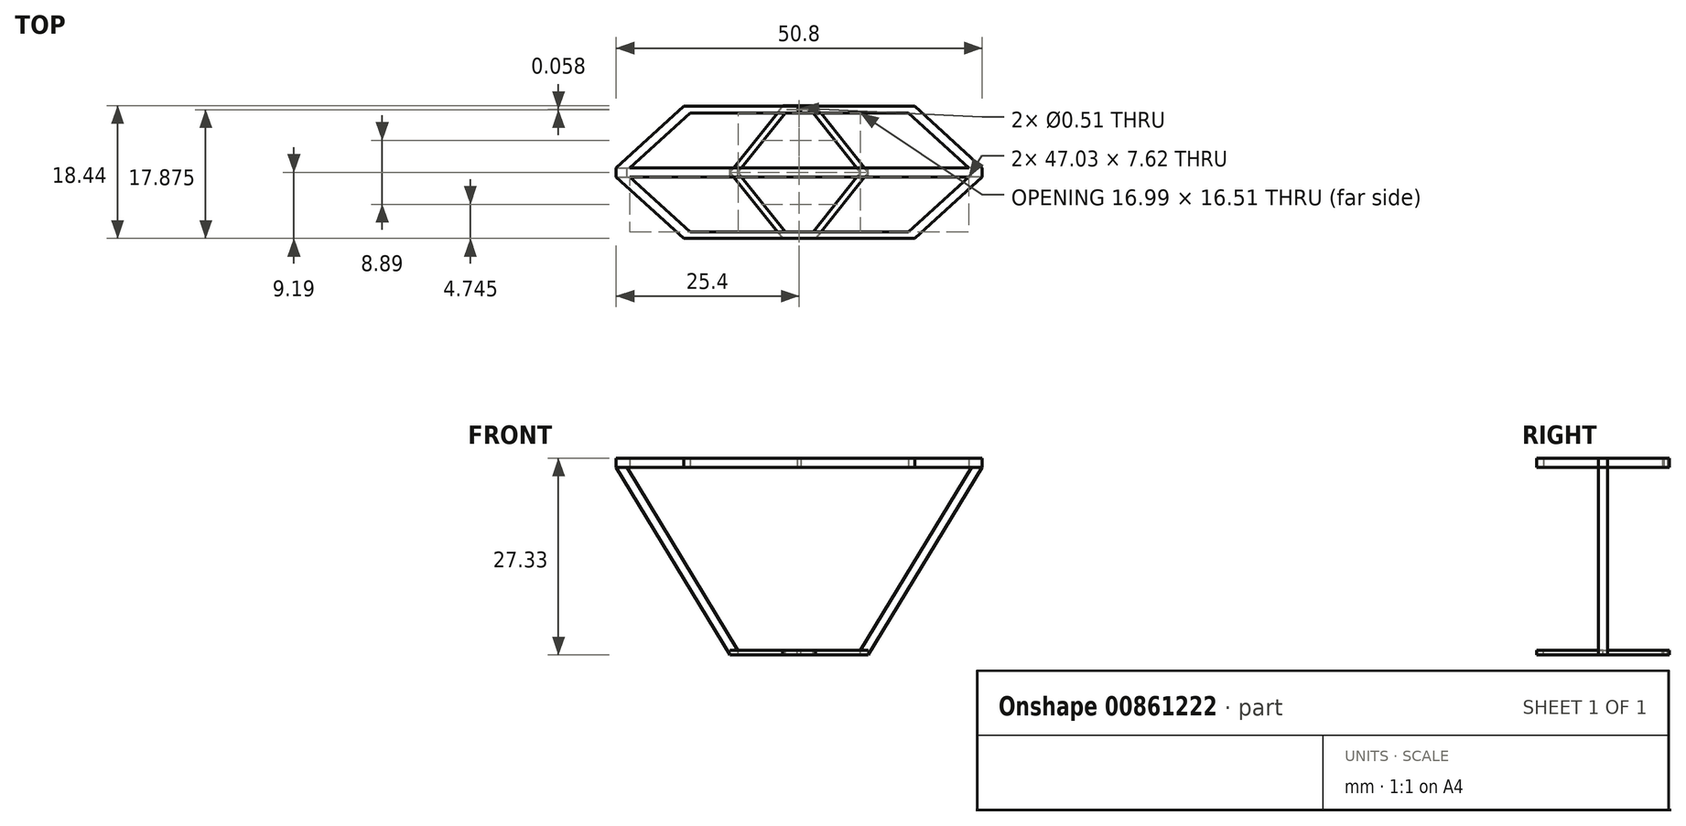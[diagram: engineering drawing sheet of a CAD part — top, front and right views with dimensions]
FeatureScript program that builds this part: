
annotation { "Feature Type Name" : "Feature", "Feature Type Description" : "" }
export const myFeature = defineFeature(function(context is Context, id is Id, definition is map)
    precondition{}
    {
        {
            var Q0;
            Q0=qCreatedBy(makeId("Top.planeOp"),FACE);
            var sketch = newSketch(context, id + "F0", { "sketchPlane" : qUnion([Q0])});
            skLineSegment(sketch, "E0.bottom", {"start": v(23.52, -0.63) * mm, "end": v(-23.52, -0.64) * mm});
            skLineSegment(sketch, "E0.top", {"start": v(23.52, 0.64) * mm, "end": v(-23.52, 0.63) * mm});
            skLineSegment(sketch, "E0.left", {"start": v(25.4, -0.63) * mm, "end": v(25.4, 0.64) * mm});
            skLineSegment(sketch, "E0.right", {"start": v(-25.4, -0.64) * mm, "end": v(-25.4, 0.63) * mm});
            skPoint(sketch, "E0.middle", {"position": v(0, 0) * mm});
            skLineSegment(sketch, "E1", {"start": v(25.4, 0.63) * mm, "end": v(16.02, 9.2) * mm});
            skLineSegment(sketch, "E2", {"start": v(23.52, 0.63) * mm, "end": v(15.16, 8.26) * mm});
            skLineSegment(sketch, "E3", {"start": v(-23.52, 0.63) * mm, "end": v(-15.16, 8.26) * mm});
            skLineSegment(sketch, "E4", {"start": v(-25.4, 0.63) * mm, "end": v(-16.02, 9.2) * mm});
            skLineSegment(sketch, "E5", {"start": v(-15.16, 8.26) * mm, "end": v(15.16, 8.25) * mm});
            skLineSegment(sketch, "E6", {"start": v(16.02, 9.2) * mm, "end": v(-16.02, 9.2) * mm});
            skLineSegment(sketch, "E7", {"start": v(-23.52, -0.63) * mm, "end": v(-15.16, -8.26) * mm});
            skLineSegment(sketch, "E8", {"start": v(-25.4, -0.63) * mm, "end": v(-16.02, -9.2) * mm});
            skLineSegment(sketch, "E9", {"start": v(25.4, -0.63) * mm, "end": v(16.02, -9.2) * mm});
            skLineSegment(sketch, "E10", {"start": v(23.52, -0.63) * mm, "end": v(15.16, -8.25) * mm});
            skLineSegment(sketch, "E11", {"start": v(-15.16, -8.26) * mm, "end": v(15.16, -8.25) * mm});
            skLineSegment(sketch, "E12", {"start": v(-16.02, -9.2) * mm, "end": v(16.02, -9.2) * mm});
            skCircle(sketch, "E13", {"center": v(0, 8.69) * mm, "radius": 0.25 * mm});
            skSolve(sketch);
        }
        {
            var Q0;
            Q0 = qSketchRegion(id + "F0", true);
            extrude(context, id + "F1", {"entities" : qUnion([Q0]), "depth" : 1.27 * mm, "offsetDistance" : 25.4 * mm});
        }
        {
            var Q0;
            Q0=qCreatedBy(makeId("Front.planeOp"),FACE);
            var sketch = newSketch(context, id + "F2", { "sketchPlane" : qUnion([Q0])});
            skLineSegment(sketch, "E14", {"start": v(-25.4, 0) * mm, "end": v(-9.59, -26.06) * mm});
            skLineSegment(sketch, "E15", {"start": v(-23.91, 0) * mm, "end": v(-8.5, -25.4) * mm});
            skLineSegment(sketch, "E16", {"start": v(-25.4, 0) * mm, "end": v(-23.91, 0) * mm});
            skLineSegment(sketch, "E17", {"start": v(25.4, 0) * mm, "end": v(9.59, -26.06) * mm});
            skLineSegment(sketch, "E18", {"start": v(23.91, 0) * mm, "end": v(8.5, -25.4) * mm});
            skLineSegment(sketch, "E19", {"start": v(25.4, 0) * mm, "end": v(23.91, 0) * mm});
            skLineSegment(sketch, "E20", {"start": v(-8.5, -25.4) * mm, "end": v(8.5, -25.4) * mm});
            skLineSegment(sketch, "E21", {"start": v(-9.59, -26.06) * mm, "end": v(9.59, -26.06) * mm});
            skSolve(sketch);
        }
        {
            var Q0;
            Q0 = qSketchRegion(id + "F2", true);
            extrude(context, id + "F3", {"entities" : qUnion([Q0]), "endBound" : BoundingType.SYMMETRIC, "depth" : 1.27 * mm, "offsetDistance" : 25.4 * mm});
        }
        {
            var Q0;
            Q0=qCreatedBy(makeId("Top.planeOp"),FACE);
            cPlane(context, id + "F4", {"entities" : qUnion([Q0]), "cplaneType" : CPlaneType.OFFSET, "offset" : 25.4 * mm, "oppositeDirection" : true, "width" : 152.4 * mm, "height" : 152.4 * mm});
        }
        {
            var Q0;
            Q0=qCreatedBy(id+"F4.planeOp",FACE);
            var sketch = newSketch(context, id + "F5", { "sketchPlane" : qUnion([Q0])});
            skLineSegment(sketch, "E22", {"start": v(8.5, 0) * mm, "end": v(1.93, 8.26) * mm});
            skLineSegment(sketch, "E23", {"start": v(9.59, 0) * mm, "end": v(2.6, 8.78) * mm});
            skLineSegment(sketch, "E24", {"start": v(-8.5, 0) * mm, "end": v(-1.93, 8.26) * mm});
            skLineSegment(sketch, "E25", {"start": v(-9.59, 0) * mm, "end": v(-3.02, 8.26) * mm});
            skLineSegment(sketch, "E26", {"start": v(-1.93, 8.26) * mm, "end": v(1.93, 8.26) * mm});
            skLineSegment(sketch, "E27", {"start": v(2.6, 8.78) * mm, "end": v(2.23, 9.25) * mm});
            skLineSegment(sketch, "E28", {"start": v(-0.69, 9.25) * mm, "end": v(2.23, 9.25) * mm});
            skLineSegment(sketch, "E29", {"start": v(3.02, 8.25) * mm, "end": v(2.6, 8.78) * mm});
            skLineSegment(sketch, "E30", {"start": v(9.59, 0) * mm, "end": v(2.6, -8.79) * mm});
            skLineSegment(sketch, "E31", {"start": v(8.5, 0) * mm, "end": v(1.93, -8.26) * mm});
            skLineSegment(sketch, "E32", {"start": v(-8.5, 0) * mm, "end": v(-1.93, -8.26) * mm});
            skLineSegment(sketch, "E33", {"start": v(-9.59, 0) * mm, "end": v(-2.6, -8.8) * mm});
            skLineSegment(sketch, "E34", {"start": v(-1.93, -8.26) * mm, "end": v(1.93, -8.26) * mm});
            skLineSegment(sketch, "E35", {"start": v(-0.69, 9.25) * mm, "end": v(-2.23, 9.25) * mm});
            skLineSegment(sketch, "E36", {"start": v(-3.29, 7.93) * mm, "end": v(-2.23, 9.25) * mm});
            skLineSegment(sketch, "E37", {"start": v(3.2, -8.04) * mm, "end": v(2.28, -9.2) * mm});
            skLineSegment(sketch, "E38", {"start": v(-2.89, -8.44) * mm, "end": v(-2.3, -9.19) * mm});
            skLineSegment(sketch, "E39", {"start": v(-2.3, -9.19) * mm, "end": v(2.28, -9.2) * mm});
            skCircle(sketch, "E40", {"center": v(0, 8.74) * mm, "radius": 0.25 * mm});
            skSolve(sketch);
        }
        {
            var Q0;
            Q0 = qSketchRegion(id + "F5", true);
            extrude(context, id + "F6", {"entities" : qUnion([Q0]), "oppositeDirection" : true, "depth" : 0.66 * mm, "offsetDistance" : 25.4 * mm});
        }
    });
